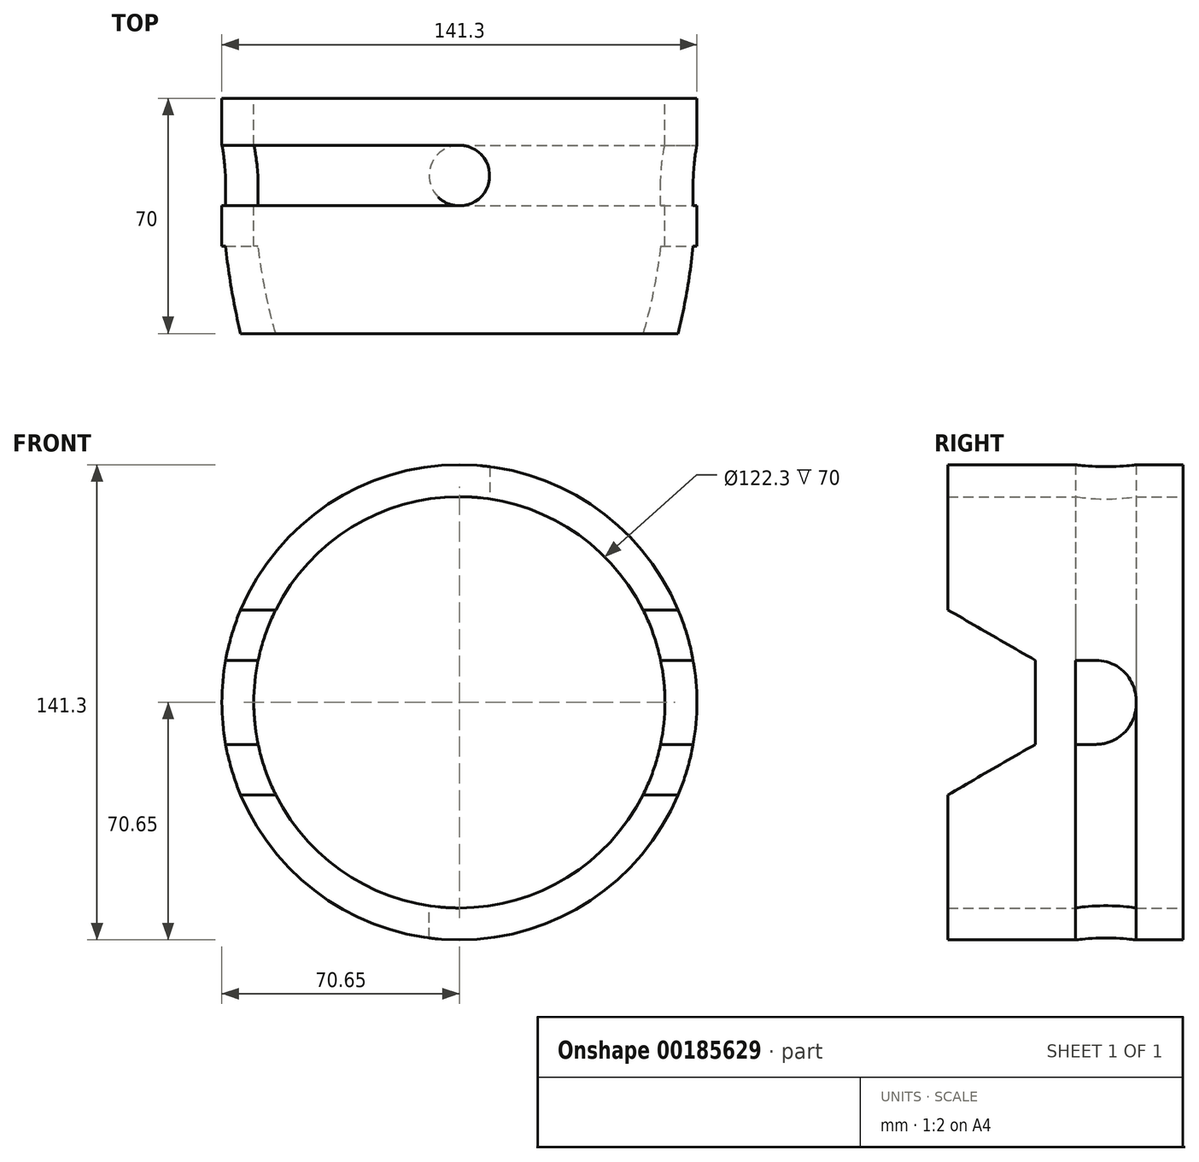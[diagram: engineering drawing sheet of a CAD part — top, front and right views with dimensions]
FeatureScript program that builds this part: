
annotation { "Feature Type Name" : "Feature", "Feature Type Description" : "" }
export const myFeature = defineFeature(function(context is Context, id is Id, definition is map)
    precondition{}
    {
        {
            var Q0;
            Q0=qCreatedBy(makeId("Front.planeOp"),FACE);
            var sketch = newSketch(context, id + "F0", { "sketchPlane" : qUnion([Q0])});
            skCircle(sketch, "E0", {"center": v(0, 0) * mm, "radius": 1794.5 * mm});
            skCircle(sketch, "E1", {"center": v(0, 0) * mm, "radius": 70.65 * mm});
            skSolve(sketch);
        }
        {
            var Q0;
            Q0=makeQuery(id+"F0.imprint","IMPRINT",FACE,{"disambiguationData":[TD([[makeQuery(id+"F0.imprint","IMPRINT",EDGE,{"derivedFrom":sQuery(id+"F0.wireOp",EDGE,"E1")}),1.0]])]});
            var Q1;
            Q1=sQuery(id+"F0.wireOp",EDGE,"E1");
            extrude(context, id + "F1", {"entities" : qUnion([Q0]), "surfaceEntities" : qUnion([Q1]), "depth" : 70 * mm});
        }
        {
            var Q0;
            Q0=makeQuery(id+"F1.opExtrude","CAP_FACE",FACE,{"disambiguationData":[OSD([sQuery(id+"F0.wireOp",EDGE,"E1")])],"isStart":false});
            var Q1;
            Q1=makeQuery(id+"F1.opExtrude","CAP_FACE",FACE,{"disambiguationData":[OSD([sQuery(id+"F0.wireOp",EDGE,"E1")])],"isStart":true});
            var Q2;
            Q2=makeQuery(id+"F1.opExtrude","SWEPT_BODY",BODY,{"disambiguationData":[OSD([sQuery(id+"F0.wireOp",EDGE,"E1")])]});
            shell(context, id + "F2", {"entities" : qUnion([Q0, Q1]), "parts" : qUnion([Q2]), "thickness" : 9.5 * mm});
        }
        {
            var Q0;
            Q0=qCreatedBy(makeId("Right.planeOp"),FACE);
            var sketch = newSketch(context, id + "F3", { "sketchPlane" : qUnion([Q0])});
            skLineSegment(sketch, "E2.bottom", {"start": v(-32, 12.5) * mm, "end": v(-26, 12.5) * mm});
            skLineSegment(sketch, "E2.top", {"start": v(-32, -12.5) * mm, "end": v(-26, -12.5) * mm});
            skLineSegment(sketch, "E2.left", {"start": v(-70, 12.5) * mm, "end": v(-70, -12.5) * mm});
            skLineSegment(sketch, "E2.right", {"start": v(-14, 0.5) * mm, "end": v(-14, -0.5) * mm});
            skPoint(sketch, "E3.visualSharp", {"position": v(-14, 12.5) * mm});
            skArc(sketch, "E3.filletArc", {"start": v(-14, 0.5) * mm, "mid": v(-17.51, 8.99) * mm, "end": v(-26, 12.5) * mm});
            skPoint(sketch, "E4.visualSharp", {"position": v(-14, -12.5) * mm});
            skArc(sketch, "E4.filletArc", {"start": v(-26, -12.5) * mm, "mid": v(-17.51, -8.99) * mm, "end": v(-14, -0.5) * mm});
            skLineSegment(sketch, "E5", {"start": v(-70, -27.5) * mm, "end": v(-70, -12.5) * mm});
            skLineSegment(sketch, "E6", {"start": v(-70, 27.5) * mm, "end": v(-44.02, 12.5) * mm});
            skLineSegment(sketch, "E7", {"start": v(-70, -27.5) * mm, "end": v(-44.02, -12.5) * mm});
            skLineSegment(sketch, "E8.trimOffspring", {"start": v(-70, 12.5) * mm, "end": v(-70, 27.5) * mm});
            skLineSegment(sketch, "E9", {"start": v(-44.02, 12.5) * mm, "end": v(-44.02, -12.5) * mm});
            skLineSegment(sketch, "E10", {"start": v(-32, 12.5) * mm, "end": v(-32, -12.5) * mm});
            skSolve(sketch);
        }
        {
            var Q0;
            Q0=qSketchRegion(id+"F3",true);
            extrude(context, id + "F4", {"entities" : qUnion([Q0]), "operationType" : NewBodyOperationType.REMOVE, "endBound" : BoundingType.THROUGH_ALL, "oppositeDirection" : true, "depth" : 25 * mm, "hasSecondDirection" : true, "secondDirectionBound" : SecondDirectionBoundingType.THROUGH_ALL, "secondDirectionOppositeDirection" : false, "secondDirectionDepth" : 25 * mm});
        }
        {
            var Q0;
            Q0=qCreatedBy(makeId("Top.planeOp"),FACE);
            var sketch = newSketch(context, id + "F5", { "sketchPlane" : qUnion([Q0])});
            skLineSegment(sketch, "E11.bottom", {"start": v(0, -32) * mm, "end": v(79.68, -32) * mm});
            skLineSegment(sketch, "E11.top", {"start": v(0, -14) * mm, "end": v(79.68, -14) * mm});
            skLineSegment(sketch, "E11.right", {"start": v(79.68, -32) * mm, "end": v(79.68, -14) * mm});
            skLineSegment(sketch, "E12", {"start": v(-9, -23.1) * mm, "end": v(-9, -23.1) * mm});
            skPoint(sketch, "E13.visualSharp", {"position": v(-8.9, -32) * mm});
            skArc(sketch, "E13.filletArc", {"start": v(-9, -23.1) * mm, "mid": v(-6.33, -29.4) * mm, "end": v(0, -32) * mm});
            skPoint(sketch, "E14.visualSharp", {"position": v(-9.1, -14) * mm});
            skArc(sketch, "E14.filletArc", {"start": v(0, -14) * mm, "mid": v(-6.4, -16.67) * mm, "end": v(-9, -23.1) * mm});
            skSolve(sketch);
        }
        {
            var Q0;
            Q0=qSketchRegion(id+"F5",true);
            extrude(context, id + "F6", {"entities" : qUnion([Q0]), "operationType" : NewBodyOperationType.REMOVE, "endBound" : BoundingType.THROUGH_ALL, "oppositeDirection" : true, "depth" : 25 * mm});
        }
        {
            var Q0;
            Q0=qCreatedBy(makeId("Top.planeOp"),FACE);
            var sketch = newSketch(context, id + "F7", { "sketchPlane" : qUnion([Q0])});
            skLineSegment(sketch, "E15.bottom", {"start": v(0, -32) * mm, "end": v(-108.62, -32) * mm});
            skLineSegment(sketch, "E15.top", {"start": v(0, -14) * mm, "end": v(-108.62, -14) * mm});
            skLineSegment(sketch, "E15.left", {"start": v(9, -23) * mm, "end": v(9, -23) * mm});
            skLineSegment(sketch, "E15.right", {"start": v(-108.62, -32) * mm, "end": v(-108.62, -14) * mm});
            skPoint(sketch, "E16.visualSharp", {"position": v(9, -32) * mm});
            skArc(sketch, "E16.filletArc", {"start": v(0, -32) * mm, "mid": v(6.36, -29.36) * mm, "end": v(9, -23) * mm});
            skPoint(sketch, "E17.visualSharp", {"position": v(9, -14) * mm});
            skArc(sketch, "E17.filletArc", {"start": v(9, -23) * mm, "mid": v(6.36, -16.64) * mm, "end": v(0, -14) * mm});
            skSolve(sketch);
        }
        {
            var Q0;
            Q0=qSketchRegion(id+"F7",true);
            extrude(context, id + "F8", {"entities" : qUnion([Q0]), "operationType" : NewBodyOperationType.REMOVE, "endBound" : BoundingType.THROUGH_ALL, "depth" : 25 * mm});
        }
    });
